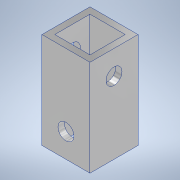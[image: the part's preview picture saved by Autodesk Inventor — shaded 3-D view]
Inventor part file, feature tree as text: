
AUTODESK INVENTOR PART (.ipt)
format: ipt  version: 2020.3 (Build 243373000, 373)  size: 121,856 bytes
history: native  units: mm
features: sketch x3, hole x2, other x1, extrude x1
ambient origin geometry x8: Origin, YZ Plane, XZ Plane, XY Plane, X Axis, Y Axis, Z Axis, Center Point
bodies: Body1 (feature_tree)
feature tree (7):
  other  "ソリッド1"
  extrude  "押し出し1"  Depth=9.0mm
  hole  "穴1"  [1 undecoded]
  hole  "穴2"  [1 undecoded]
  sketch  "スケッチ1"
  sketch  "スケッチ2"
  sketch  "スケッチ3"
note: 2 required parameter values undecoded (feature->parameter linkage not recoverable at this tier; creation-order binding heuristic only, values carry confidence <= 0.55)
